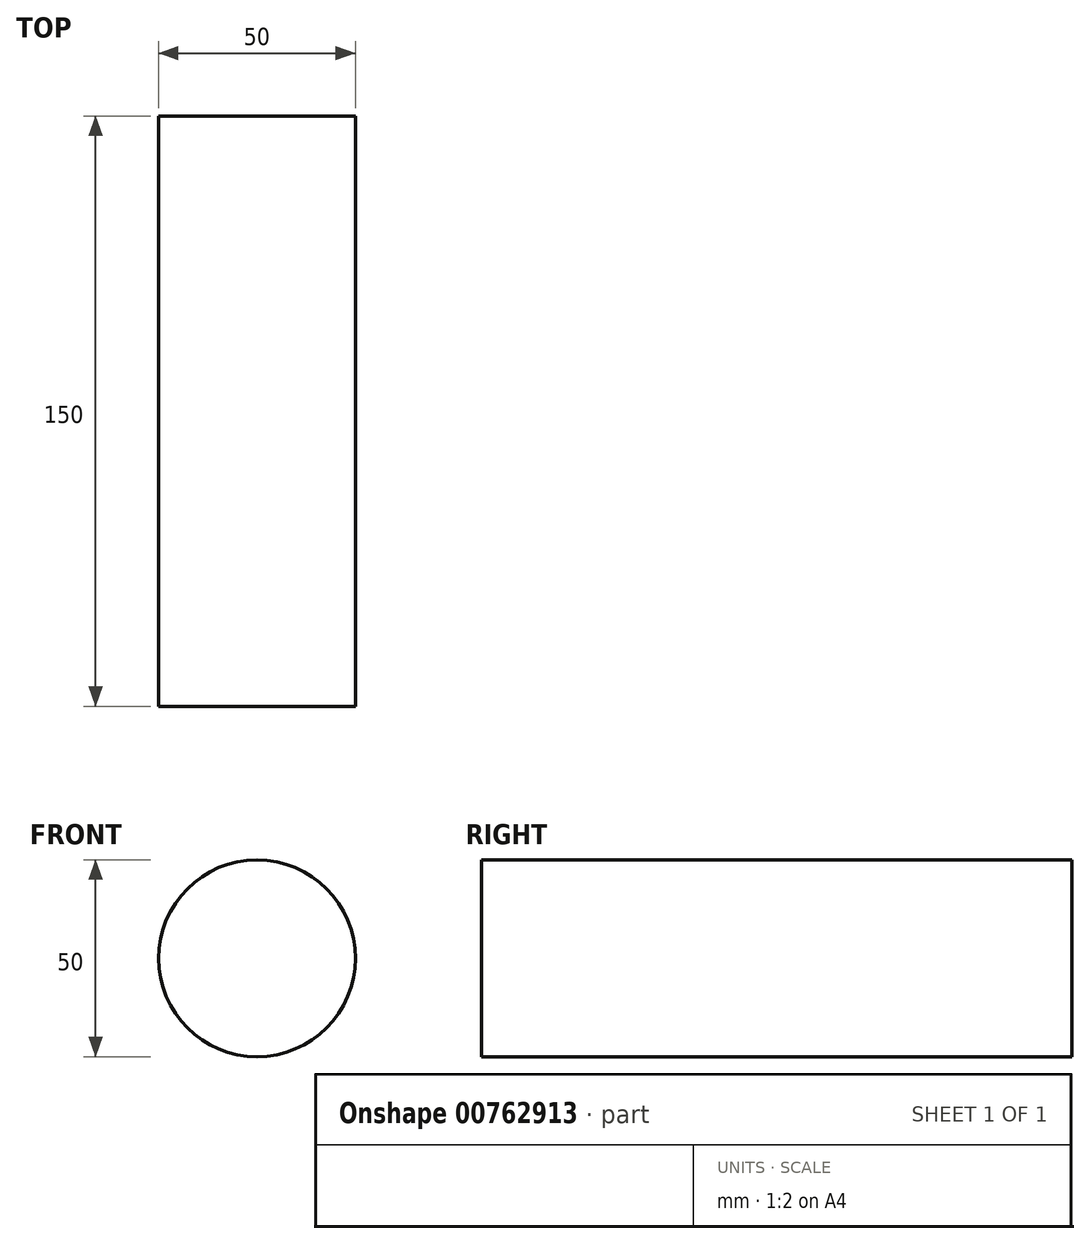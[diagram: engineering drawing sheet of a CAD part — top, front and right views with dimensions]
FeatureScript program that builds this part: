
annotation { "Feature Type Name" : "Feature", "Feature Type Description" : "" }
export const myFeature = defineFeature(function(context is Context, id is Id, definition is map)
    precondition{}
    {
        {
            var Q0;
            Q0=qCreatedBy(makeId("Front.planeOp"),FACE);
            var sketch = newSketch(context, id + "F0", { "sketchPlane" : qUnion([Q0])});
            skCircle(sketch, "E0", {"center": v(0, 0) * mm, "radius": 25 * mm});
            skSolve(sketch);
        }
        {
            var Q0;
            Q0 = qSketchRegion(id + "F0", true);
            extrude(context, id + "F1", {"entities" : qUnion([Q0]), "depth" : 150 * mm, "offsetDistance" : 25.4 * mm});
        }
    });
